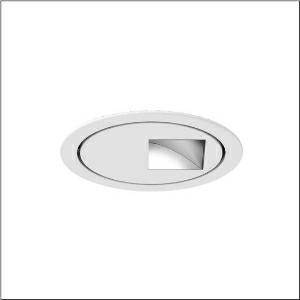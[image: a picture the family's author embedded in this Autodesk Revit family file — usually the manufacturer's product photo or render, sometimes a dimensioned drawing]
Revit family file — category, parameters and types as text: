
# Revit family: lunis_11_mini_round_51dk11b72wm21
name_source: partatom
category: Lighting Fixtures
units: mm (PartAtom-declared; Revit-internal decimal feet)

## family parameters
Cut with Voids When Loaded = No
Host = Face
Light Source = No
Part Type = Normal
Room Calculation Point = No
Round Connector Dimension = Use Diameter
Shared = No

## types (1)
- Lunis 11 mini round (1 x LED 3000K / CRI = 90 (unbekannt), 1930 lm, 3000K)
    Apparent Load = 28 VA
    CIE Flux Codes = 44 77 97 100 100
    Color Rendering = 90
    Color Temperature = 3000K
    Default Elevation = 1800 mm
    Description = Lunis 11 mini round, downlight, light control with wallwasher, of highly reflective aluminium, highly specular, light emission: direct distribution, LED rated luminous flux: 1.930lm, light colour: 930, control gear: ECG, with terminal, 3-pole, mains connection: 220..230V, AC/DC, 0/50..60Hz, LED module, luminaire module, of aluminium, highly specular, white, diameter: 176mm, clamping range: 1..40mm, recessing ring, of plastic, traffic white (RAL 9016), protection rating (complete): IP20, insulation class (complete): insulation class II (safety insulation), certification: CE, permissible ambient temperature for indoor applications: 0..+35°C, packaging unit: 1 piece
    Height = 0 mm  [stored 0 ft]
    Lamp = 1 x LED 3000K / CRI >= 90 (unbekannt)
    Lamp Light Flux = 1930 lm
    Lamp count = 1
    Length = 176 mm
    Luminous efficacy = 69 lm/W
    Manufacturer = Siteco
    ModVariant = No
    Model = 51DK11B72WM21
    Mounting Place = Ceiling
    Mounting Type = Recessed
    Number of Poles = 1
    OnlyDefault = Yes
    Power Factor = 1
    Product Name = Lunis 11 mini round
    Product group = downlight
    ProductGroupID = 400
    Protection Class = Protection class II
    Protection Degree = IP 20
    RLX_Detail_Level = 1
    RLX_Emergency_Light_Flux = 0 lm
    RLX_Emergency_Type = 0
    RLX_Emergency_Type_DB = No
    RlxData = <blob elided: 59185 chars, md5=0ef2da2c>
    Socket = socket
    Standby Power = 0 W
    System Light Flux = 1930 lm
    System Power = 28 W
    Type Comments = Product without accessories
    Type Image = l_1004772.jpg
    URL = http://relux.com
    VarID = ---
    Voltage = 0 V
    Weight = 0.00 kg
    Width = 176 mm

note: [stored X ft] marks values corroborated as IEEE doubles in the binary element streams (Revit-internal decimal feet)

## geometry (parser evidence)
native form markers: Blend x4, Sweep x12
no freeform markers — native parametric forms only
